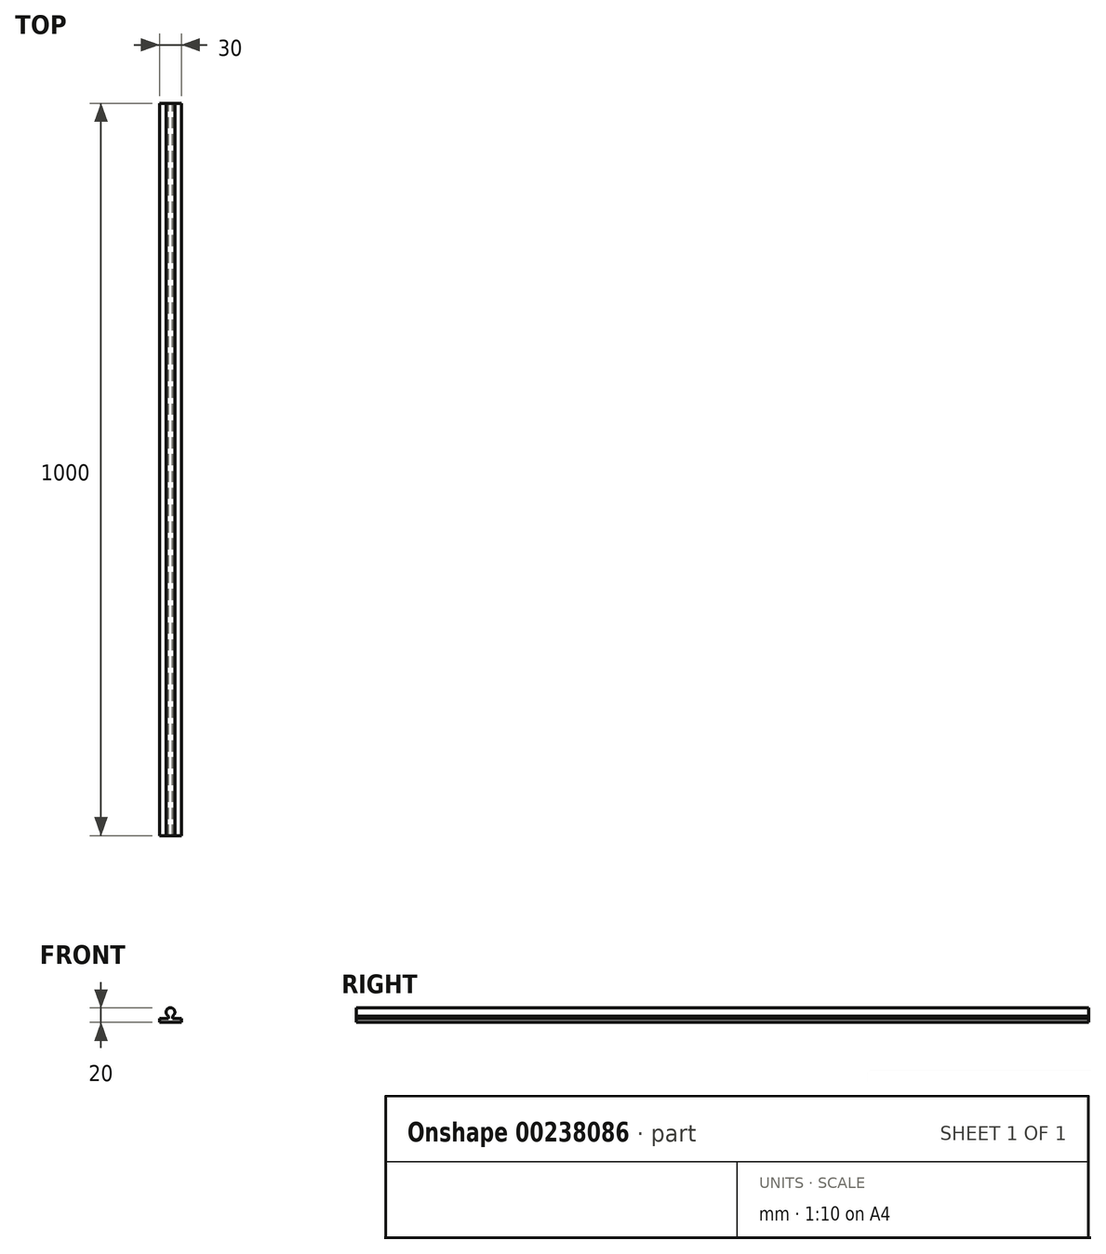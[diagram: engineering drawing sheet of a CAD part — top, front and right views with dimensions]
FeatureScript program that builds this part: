
annotation { "Feature Type Name" : "Feature", "Feature Type Description" : "" }
export const myFeature = defineFeature(function(context is Context, id is Id, definition is map)
    precondition{}
    {
        {
            var Q0;
            Q0=qCreatedBy(makeId("Front.planeOp"),FACE);
            var sketch = newSketch(context, id + "F0", { "sketchPlane" : qUnion([Q0])});
            skLineSegment(sketch, "E0", {"start": v(0, 0) * mm, "end": v(-15, 0) * mm});
            skLineSegment(sketch, "E1", {"start": v(-15, 0) * mm, "end": v(-15, 5) * mm});
            skLineSegment(sketch, "E2", {"start": v(-15, 5) * mm, "end": v(-3, 5) * mm});
            skArc(sketch, "E3", {"start": v(0, 20) * mm, "mid": v(-5.8, 15.55) * mm, "end": v(-3, 8.8) * mm});
            skLineSegment(sketch, "E4", {"start": v(-3, 5) * mm, "end": v(-3, 8.8) * mm});
            skPoint(sketch, "E5.start.orphan", {"position": v(0, 5) * mm});
            skLineSegment(sketch, "E6.MirrorCS", {"start": v(3, 5) * mm, "end": v(3, 8.8) * mm});
            skLineSegment(sketch, "E7.MirrorCS", {"start": v(15, 0) * mm, "end": v(15, 5) * mm});
            skLineSegment(sketch, "E8.MirrorCS", {"start": v(15, 5) * mm, "end": v(3, 5) * mm});
            skLineSegment(sketch, "E9.MirrorCS", {"start": v(0, 0) * mm, "end": v(15, 0) * mm});
            skArc(sketch, "E10.MirrorCS", {"start": v(0, 20) * mm, "mid": v(5.8, 15.55) * mm, "end": v(3, 8.8) * mm});
            skSolve(sketch);
        }
        {
            var Q0;
            Q0=makeQuery(id+"F0.imprint","IMPRINT",FACE,{"disambiguationData":[TD([[makeQuery(id+"F0.imprint","IMPRINT",EDGE,{"derivedFrom":sQuery(id+"F0.wireOp",EDGE,"E0")}),-1.0]])]});
            extrude(context, id + "F1", {"entities" : qUnion([Q0]), "depth" : 1000 * mm});
        }
    });
